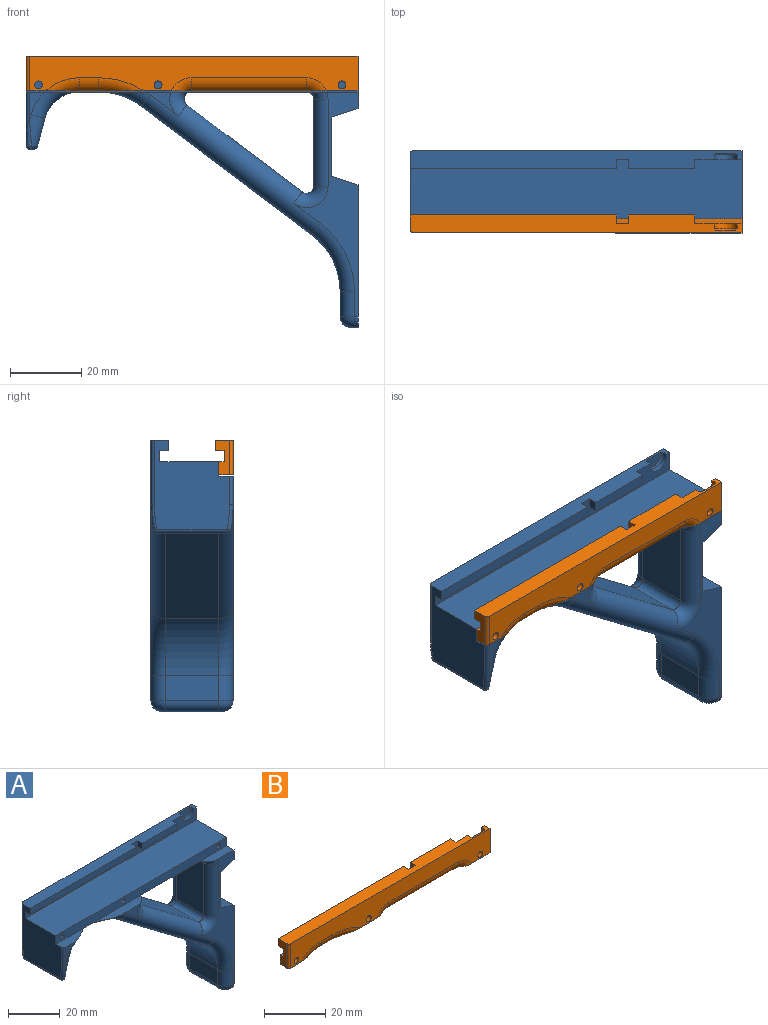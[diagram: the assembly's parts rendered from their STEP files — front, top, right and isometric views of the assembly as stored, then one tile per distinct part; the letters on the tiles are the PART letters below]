
ASSEMBLY  parts=2 mates=1
PART A: 85 faces, bbox 99.9x24.1x76.3 mm
  f0: plane 8.01x4.16mm, normal (0,-1,0), area 12.6mm2, adj f28,f29,f57,f70
  f1: plane 9.08x6.79mm, normal (0,-1,0), area 18.1mm2, adj f30,f31,f56,f72
  f2: plane 93x16.5mm, normal (0,0,1), area 1534.5mm2, adj f3,f4,f5,f73
  f3: plane 23x14.6mm, normal (1,0,0), area 196.8mm2, adj f2,f5,f6,f7,f16,f34,f71,f73
  f4: plane 25.19x21.19mm, normal (-1,0,0), area 400.5mm2, adj f2,f5,f34,f35,f37,f57,f58,f62
  f5: plane 93x6mm, normal (0,-1,0), area 316mm2, adj f2,f3,f4,f34,f35,f36,f38,f39
  f6: plane 63x18.01mm, normal (0,-1,0), area 280.7mm2, adj f3,f13,f14,f15,f16,f31,f32,f33
  f7: plane 92x73mm, normal (0,1,0), area 984.6mm2, adj f3,f13,f14,f15,f16,f21,f22,f23
  f8: cylinder r=20mm len=15mm, axis (0,1,0), area 193.8mm2, adj f9,f20,f24,f30
  f9: plane 47.7x35.97mm, normal (-0.6,0,-0.8), area 896.1mm2, adj f8,f10,f25,f31
  f10: cylinder r=20mm len=15.97mm, axis (0,1,0), area 277.4mm2, adj f9,f11,f26,f32
  f11: plane 15x7.03mm, normal (-1,0,0), area 105.5mm2, adj f10,f27,f33,f82
  f12: plane 17x2mm, normal (0,0,-1), area 33.6mm2, adj f13,f80,f81,f82,f83,f84
  f13: plane 40x23mm, normal (1,0,0), area 916.1mm2, adj f6,f7,f12,f14,f80,f84
  f14: plane 23x7.4mm, normal (0.31,0,0.95), area 178.9mm2, adj f6,f7,f13,f15
  f15: plane 23x16.6mm, normal (1,0,0), area 381.8mm2, adj f6,f7,f14,f16
  f16: plane 23x7.4mm, normal (0.31,0,-0.95), area 178.9mm2, adj f3,f6,f7,f15
  f17: plane 19.79x1.23mm, normal (0,0,-1), area 22.6mm2, adj f59,f61,f62,f63
  f18: plane 15x7.85mm, normal (0.97,0,-0.26), area 121.9mm2, adj f19,f21,f28,f61
  f19: cylinder r=10mm len=15mm, axis (0,1,0), area 196.3mm2, adj f18,f20,f22,f29
  f20: plane 15x5.34mm, normal (0,0,-1), area 80.2mm2, adj f8,f19,f23,f73
  f21: cylinder r=4mm len=9.19mm, axis (0.26,0,0.97), area 44mm2, adj f7,f18,f22,f63,f66
  f22: torus R=14mm, axis (0,-1,0), area 94.2mm2, adj f7,f19,f21,f23
  f23: cylinder r=4mm len=5.34mm, axis (1,0,0), area 33.6mm2, adj f7,f20,f22,f24
  f24: torus R=24mm, axis (0,-1,0), area 87.1mm2, adj f7,f8,f23,f25
  f25: cylinder r=4mm len=52.51mm, axis (0.8,0,-0.6), area 629.8mm2, adj f7,f9,f24,f26,f42,f50,f52
  f26: torus R=24mm, axis (0,-1,0), area 124.6mm2, adj f7,f10,f25,f27
  f27: cylinder r=4mm len=7.03mm, axis (0,0,-1), area 44.2mm2, adj f7,f11,f26,f83
  f28: cylinder r=4mm len=9.19mm, axis (-0.26,0,-0.97), area 44mm2, adj f0,f18,f29,f58,f59
  f29: torus R=14mm, axis (0,-1,0), area 61.1mm2, adj f0,f19,f28,f70
  f30: torus R=24mm, axis (0,-1,0), area 42.7mm2, adj f1,f8,f31,f72
  f31: cylinder r=4mm len=52.51mm, axis (-0.8,0,0.6), area 629.8mm2, adj f1,f6,f9,f30,f32,f42,f54,f56
  f32: torus R=24mm, axis (0,-1,0), area 124.6mm2, adj f6,f10,f31,f33
  f33: cylinder r=4mm len=7.03mm, axis (0,0,1), area 44.2mm2, adj f6,f11,f32,f81
  f34: plane 93x5mm, normal (0,0,1), area 412.2mm2, adj f3,f4,f5,f7,f36,f37,f38,f40
  f35: plane 57.9x2.5mm, normal (0,0,-1), area 144.8mm2, adj f4,f5,f36,f37
  f36: plane 2.9x2.5mm, normal (1,0,0), area 7.3mm2, adj f5,f34,f35,f37
  f37: plane 57.9x2.9mm, normal (0,-1,0), area 167.9mm2, adj f4,f34,f35,f36
  f38: plane 2.9x2.5mm, normal (-1,0,0), area 7.3mm2, adj f5,f34,f39,f41
  f39: plane 18.6x2.5mm, normal (0,0,-1), area 46.5mm2, adj f5,f38,f40,f41
  f40: plane 2.9x2.5mm, normal (1,0,0), area 7.3mm2, adj f5,f34,f39,f41
  f41: plane 18.6x2.9mm, normal (0,-1,0), area 53.9mm2, adj f34,f38,f39,f40
  f42: plane 32.34x24.39mm, normal (0.6,0,0.8), area 607.6mm2, adj f25,f31,f45,f47
  f43: plane 24.39x15mm, normal (-1,0,0), area 365.8mm2, adj f45,f46,f48,f53
  f44: plane 32.34x15mm, normal (0,0,-1), area 485.1mm2, adj f46,f47,f51,f73
  f45: cylinder r=2mm len=15mm, axis (0,1,0), area 66.5mm2, adj f42,f43,f50,f54
  f46: cylinder r=2mm len=15mm, axis (0,1,0), area 47.1mm2, adj f43,f44,f49,f55
  f47: cylinder r=2mm len=15mm, axis (0,1,0), area 74.9mm2, adj f42,f44,f52,f56
  f48: cylinder r=4mm len=24.39mm, axis (0,0,1), area 153.2mm2, adj f7,f43,f49,f50
  f49: torus R=6mm, axis (0,-1,0), area 34.1mm2, adj f7,f46,f48,f51
  f50: torus R=6mm, axis (0,-1,0), area 48.1mm2, adj f7,f25,f45,f48
  f51: cylinder r=4mm len=32.34mm, axis (-1,0,0), area 203.2mm2, adj f7,f44,f49,f52
  f52: torus R=6mm, axis (0,-1,0), area 54.1mm2, adj f7,f25,f47,f51
  f53: cylinder r=4mm len=24.39mm, axis (0,0,-1), area 153.2mm2, adj f6,f43,f54,f55
  f54: torus R=6mm, axis (0,-1,0), area 48.1mm2, adj f6,f31,f45,f53
  f55: torus R=6mm, axis (0,-1,0), area 14.4mm2, adj f6,f46,f53,f71
  f56: torus R=6mm, axis (0,-1,0), area 34.5mm2, adj f1,f31,f47,f72
  f57: cylinder r=1mm len=8.01mm, axis (0,0,1), area 12.6mm2, adj f0,f4,f58,f70
  f58: bspline ~13.34x2.58mm, area 13.4mm2, adj f4,f28,f57,f60
  f59: bspline ~4.25x2.64mm, area 4.5mm2, adj f17,f28,f60,f61
  f60: sphere r=1mm, area 2mm2, adj f58,f59,f62
  f61: cylinder r=1mm len=15mm, axis (0,-1,0), area 19.6mm2, adj f17,f18,f59,f63
  f62: cylinder r=1mm len=19.79mm, axis (0,-1,0), area 31.1mm2, adj f4,f17,f60,f65
  f63: bspline ~3.55x2.64mm, area 4.5mm2, adj f17,f21,f61,f65
  f64: cylinder r=1mm len=18.01mm, axis (0,0,-1), area 28.3mm2, adj f4,f7,f34,f66
  f65: sphere r=1mm, area 2mm2, adj f62,f63,f66
  f66: bspline ~13.34x2.58mm, area 13.4mm2, adj f4,f21,f64,f65
  f67: cylinder r=3.25mm len=6.5mm, axis (0,-1,0), area 15.8mm2, adj f5,f34,f69
  f68: plane 5.7x3.4mm, normal (0,-1,0), area 15.9mm2, adj f34,f69
  f69: cone r=2.85mm half-angle=45deg, axis (0,-1,0), area 6mm2, adj f34,f67,f68
  f70: plane 14.96x4mm, normal (0,0,1), area 45.2mm2, adj f0,f4,f29,f57,f73
  f71: plane 14.4x4mm, normal (0,0,1), area 50.4mm2, adj f3,f6,f55,f73
  f72: plane 25.96x4.01mm, normal (0,0,1), area 76.5mm2, adj f1,f30,f56,f73
  f73: plane 93x4mm, normal (0,-1,0), area 360.6mm2, adj f2,f3,f4,f20,f44,f70,f71,f72
  f74: plane 2.2x2.2mm, normal (0,-1,0), area 3.8mm2, adj f75
  f75: cylinder r=1.1mm len=11mm, axis (0,-1,0), area 76mm2, adj f73,f74
  f76: plane 2.2x2.2mm, normal (0,-1,0), area 3.8mm2, adj f77
  f77: cylinder r=1.1mm len=11mm, axis (0,-1,0), area 76mm2, adj f73,f76
  f78: plane 2.2x2.2mm, normal (0,-1,0), area 3.8mm2, adj f79
  f79: cylinder r=1.1mm len=11mm, axis (0,-1,0), area 76mm2, adj f73,f78
  f80: cylinder r=3mm len=3mm, axis (-1,0,0), area 4.7mm2, adj f6,f12,f13,f81
  f81: torus R=1mm, axis (0,0,-1), area 21.5mm2, adj f12,f33,f80,f82
  f82: cylinder r=3mm len=15mm, axis (0,-1,0), area 70.7mm2, adj f11,f12,f81,f83
  f83: torus R=1mm, axis (0,0,-1), area 21.5mm2, adj f12,f27,f82,f84
  f84: cylinder r=3mm len=3mm, axis (1,0,0), area 4.7mm2, adj f7,f12,f13,f83
PART B: 28 faces, bbox 93x5x13.2 mm
  f0: plane 92x9.7mm, normal (0,-1,0), area 655.7mm2, adj f1,f2,f3,f4,f5,f6,f7,f10
  f1: torus R=14mm, axis (0,-1,0), area 27.7mm2, adj f0,f2,f26
  f2: cylinder r=4mm len=5.34mm, axis (-1,0,0), area 25.2mm2, adj f0,f1,f3,f26
  f3: torus R=24mm, axis (0,-1,0), area 37.1mm2, adj f0,f2,f26
  f4: torus R=6mm, axis (0,-1,0), area 16.8mm2, adj f0,f5,f26
  f5: cylinder r=4mm len=32.34mm, axis (1,0,0), area 152.8mm2, adj f0,f4,f6,f26
  f6: torus R=6mm, axis (0,-1,0), area 16.8mm2, adj f0,f5,f26
  f7: cylinder r=1mm len=9.7mm, axis (0,0,1), area 15.2mm2, adj f0,f11,f12,f26
  f8: plane 93x6mm, normal (0,1,0), area 316mm2, adj f9,f10,f11,f12,f13,f14,f15,f17
  f9: plane 93x1.5mm, normal (0,0,1), area 139.5mm2, adj f8,f10,f11,f27
  f10: plane 9.7x4mm, normal (1,0,0), area 29.8mm2, adj f0,f8,f9,f12,f26,f27
  f11: plane 9.7x4mm, normal (-1,0,0), area 27.3mm2, adj f7,f8,f9,f12,f18,f19,f26,f27
  f12: plane 93x5mm, normal (0,0,1), area 412.2mm2, adj f0,f7,f8,f10,f11,f14,f15,f16
  f13: plane 18.6x2.5mm, normal (0,0,-1), area 46.5mm2, adj f8,f14,f15,f16
  f14: plane 2.9x2.5mm, normal (-1,0,0), area 7.3mm2, adj f8,f12,f13,f16
  f15: plane 2.9x2.5mm, normal (1,0,0), area 7.3mm2, adj f8,f12,f13,f16
  f16: plane 18.6x2.9mm, normal (0,1,0), area 53.9mm2, adj f12,f13,f14,f15
  f17: plane 2.9x2.5mm, normal (1,0,0), area 7.3mm2, adj f8,f12,f18,f19
  f18: plane 57.9x2.5mm, normal (0,0,-1), area 144.8mm2, adj f8,f11,f17,f19
  f19: plane 57.9x2.9mm, normal (0,1,0), area 167.9mm2, adj f11,f12,f17,f18
  f20: cylinder r=3.25mm len=6.5mm, axis (0,1,0), area 15.8mm2, adj f8,f12,f22
  f21: plane 5.7x3.4mm, normal (0,1,0), area 15.9mm2, adj f12,f22
  f22: cone r=2.85mm half-angle=45deg, axis (0,1,0), area 6mm2, adj f12,f20,f21
  f23: cylinder r=1.1mm len=4mm, axis (0,-1,0), area 27.6mm2, adj f0,f27
  f24: cylinder r=1.1mm len=4mm, axis (0,-1,0), area 27.6mm2, adj f0,f27
  f25: cylinder r=1.1mm len=4mm, axis (0,-1,0), area 27.6mm2, adj f0,f27
  f26: plane 93x4.01mm, normal (0,0,-1), area 241.9mm2, adj f0,f1,f2,f3,f4,f5,f6,f7
  f27: plane 93x3.7mm, normal (0,1,0), area 332.7mm2, adj f9,f10,f11,f23,f24,f25,f26
PLACE A t=(-45.09,-42.78,-16.75)mm
PLACE B t=(-45.09,-42.78,-16.75)mm
MATE cylindrical A.f77 <-> B.f23  axis (0,-1,0) through (-134.59,-61.78,-18.75)mm
